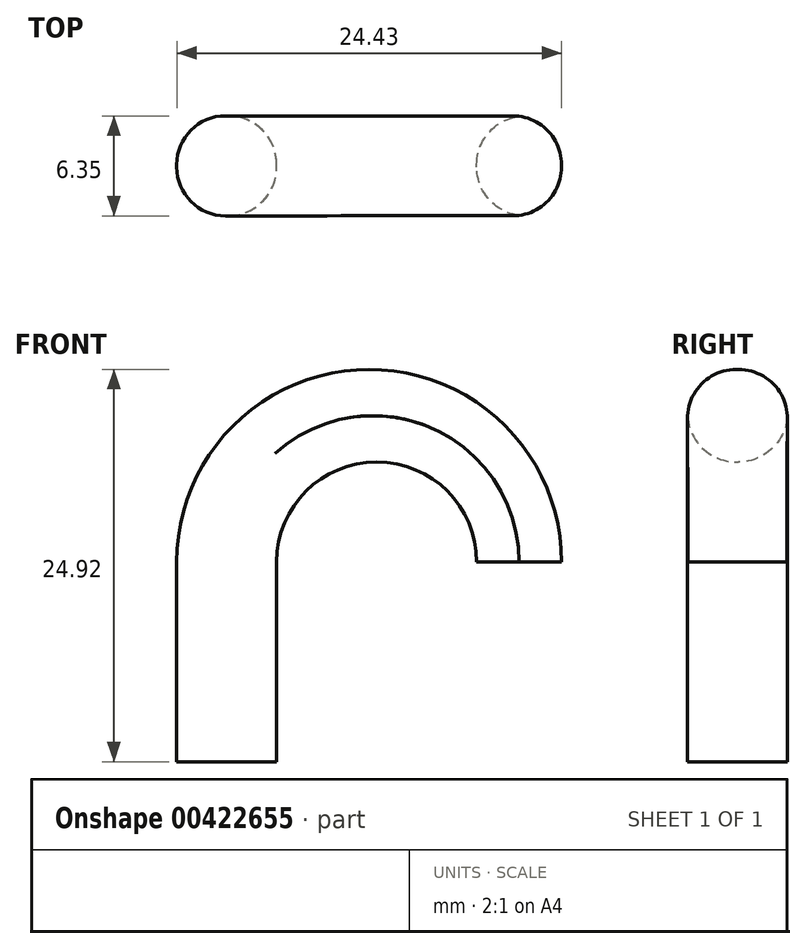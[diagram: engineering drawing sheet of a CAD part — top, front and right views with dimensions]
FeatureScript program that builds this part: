
annotation { "Feature Type Name" : "Feature", "Feature Type Description" : "" }
export const myFeature = defineFeature(function(context is Context, id is Id, definition is map)
    precondition{}
    {
        {
            var Q0;
            Q0=qCreatedBy(makeId("Front.planeOp"),FACE);
            var sketch = newSketch(context, id + "F0", { "sketchPlane" : qUnion([Q0])});
            skLineSegment(sketch, "E0", {"start": v(-45.5, 24.65) * mm, "end": v(-45.5, 11.95) * mm});
            skLineSegment(sketch, "E1", {"start": v(-45.5, 11.95) * mm, "end": v(-39.15, 11.95) * mm});
            skLineSegment(sketch, "E2", {"start": v(-39.15, 11.95) * mm, "end": v(-39.15, 24.65) * mm});
            skArc(sketch, "E3", {"start": v(-26.45, 24.65) * mm, "mid": v(-32.8, 30.99) * mm, "end": v(-39.15, 24.65) * mm});
            skArc(sketch, "E4", {"start": v(-21.07, 24.64) * mm, "mid": v(-33.28, 36.87) * mm, "end": v(-45.5, 24.65) * mm});
            skLineSegment(sketch, "E5", {"start": v(-26.45, 24.65) * mm, "end": v(-21.07, 24.64) * mm});
            skSolve(sketch);
        }
        {
            var Q0;
            Q0=makeQuery(id+"F0.imprint","IMPRINT",FACE,{"disambiguationData":[TD([[makeQuery(id+"F0.imprint","IMPRINT",EDGE,{"derivedFrom":sQuery(id+"F0.wireOp",EDGE,"E0")}),1.0]])]});
            extrude(context, id + "F1", {"entities" : qUnion([Q0]), "depth" : 6.35 * mm});
        }
        {
            var Q0;
            Q0=makeQuery(id+"F1.opExtrude","CAP_EDGE",EDGE,{"disambiguationData":[OSD([sQuery(id+"F0.wireOp",EDGE,"E0")])],"isStart":false});
            var Q1;
            Q1=makeQuery(id+"F1.opExtrude","CAP_EDGE",EDGE,{"disambiguationData":[OSD([sQuery(id+"F0.wireOp",EDGE,"E2")])],"isStart":false});
            var Q2;
            Q2=makeQuery(id+"F1.opExtrude","CAP_EDGE",EDGE,{"disambiguationData":[OSD([sQuery(id+"F0.wireOp",EDGE,"E3")])],"isStart":false});
            var Q3;
            Q3=makeQuery(id+"F1.opExtrude","CAP_EDGE",EDGE,{"disambiguationData":[OSD([sQuery(id+"F0.wireOp",EDGE,"E2")])],"isStart":true});
            var Q4;
            Q4=makeQuery(id+"F1.opExtrude","CAP_EDGE",EDGE,{"disambiguationData":[OSD([sQuery(id+"F0.wireOp",EDGE,"E4")])],"isStart":true});
            fillet(context, id + "F2", {"entities" : qUnion([Q0, Q1, Q2, Q3, Q4]), "radius" : 3.1 * mm, "tangentPropagation" : true, "allowEdgeOverflow" : false});
        }
    });
